# Revit family: PRD_FrankeWS_SntryTwlDspslBins_STRATOSSanitaryTowelAndDisposalBin_STRX611
name_source: partatom
category: Furniture
revit_build: Autodesk Revit 2018 (Build: 20190510_1515(x64)
units: mm (PartAtom-declared; Revit-internal decimal feet)

## family parameters
Cut with Voids When Loaded = No
Host = Face
OmniClass Number = 23.40.20.31.11
OmniClass Title = Bins
Room Calculation Point = No
Shared = No

## types (1)
- STRX611
    AssetType = Fixed
    BIMObjectName = PRD_AR_SanitaryTowelDisposalBins_STRATOSSanitaryTowelAndDisposalBin_STRX611
    Category = Pr_40_50_07_76, Sanitary towel disposal bins
    Color = Stainless steel
    Default Elevation = 820 mm  [stored 2.69029 ft]
    Description = Sanitary towel and disposal bin for wall mounting, stainless steel, surface satin finished, front with InoxPlus surface refinement for the reduction of finger marks and better cleaning characteristics (easy to clean), material thickness 1.5 mm, curved front cover, approx. 3.8 liter capacity, folding selfclosing lid with piano hinge, removable plastic container inside, incl. stainless steel screws and dowels.
    DurationUnit = year
    Features = stainless steel, 1.50 mm, wall mounting, 205x305x134 mm (WxHxD)
    FillingQuantity = 3.80 L
    Finish = Satin finished
    FinishAndColour = Stainless steel, satin finished
    Form = Wall mounted
    GrossWeight = 3.72 kg
    IfcExportAs = IfcFurnitureType
    IfcExportType = NOTDEFINED
    IntegralAccessories = includes mounting materials
    MainColor = Stainless steel
    Manufacturer = KWC Group AG
    ManufacturerName = KWC Group AG
    ManufacturerURL = www.kwc.com
    Material = Stainless steel
    Materials = Stainless steel 1.4301
    Model = STRX611
    ModelNumber = 2000057375
    ModelReference = STRX611
    NBSDescription = Sanitary towel disposal bins
    NBSReference = 45-35-72/350
    Name = STRATOS Sanitary towel and disposal bin STRX611
    NetWeight = 3.42 kg
    NominalDepth = 134 mm
    NominalHeight = 305 mm  [stored 1.00066 ft]
    NominalLength = 205 mm  [stored 0.672572 ft]
    NominalWidth = 205 mm  [stored 0.672572 ft]
    ProductInformation = https://pim.kwc.com
    Size = 205x305x134 mm
    Style = Sanitary towel and disposal bin
    SurfaceTreatment = InoxPlus (anti fingerprint)
    URL = www.kwc.com
    Uniclass2015Code = Pr_40_50_07_76
    Uniclass2015Title = Sanitary towel disposal bins
    Uniclass2015Version = Products v1.7
    Version = 1
    WarrantyDurationUnit = year
    WasteBinMaterial = PRD_AR_StainlessSteel_SatinFinished

note: [stored X ft] marks values corroborated as IEEE doubles in the binary element streams (Revit-internal decimal feet)

## geometry (parser evidence)
native form markers: Sweep x2
no freeform markers — native parametric forms only
